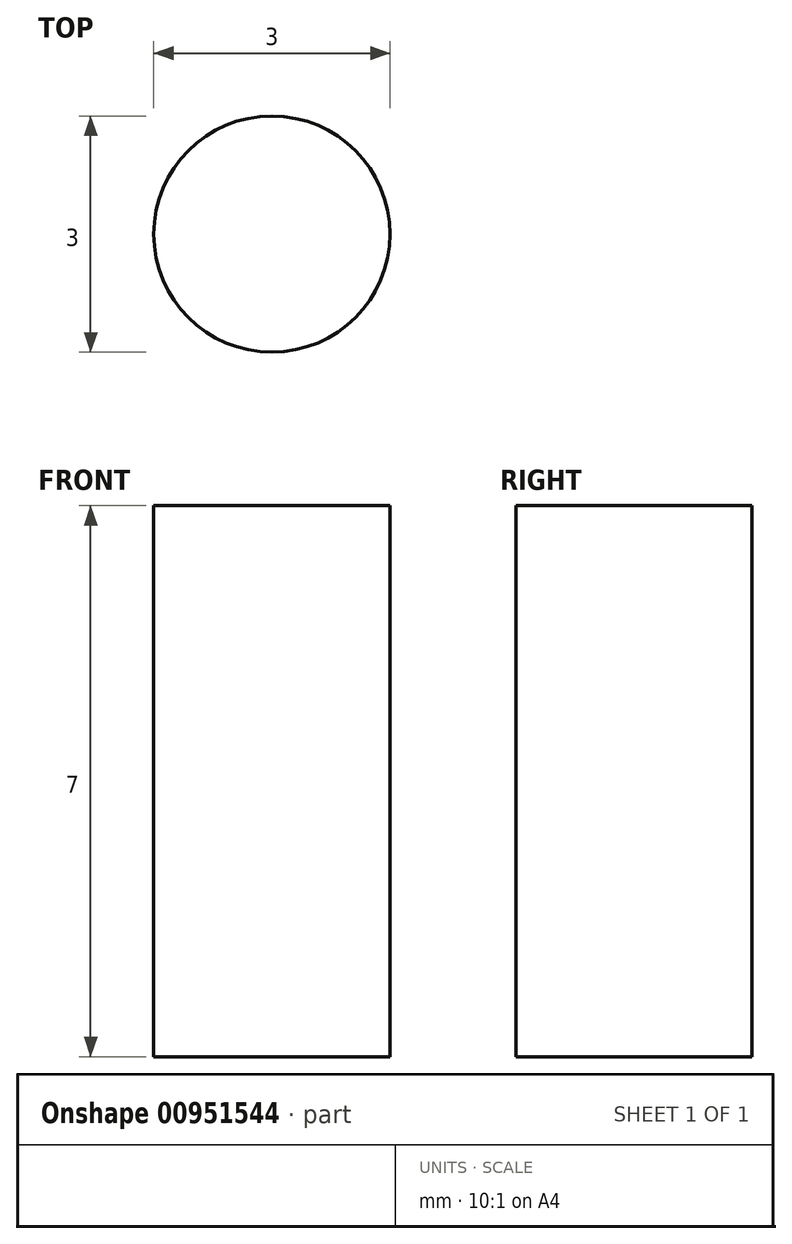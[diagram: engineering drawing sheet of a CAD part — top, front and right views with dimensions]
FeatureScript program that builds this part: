
annotation { "Feature Type Name" : "Feature", "Feature Type Description" : "" }
export const myFeature = defineFeature(function(context is Context, id is Id, definition is map)
    precondition{}
    {
        {
            var Q0;
            Q0=qCreatedBy(makeId("Top.planeOp"),FACE);
            var sketch = newSketch(context, id + "F0", { "sketchPlane" : qUnion([Q0])});
            skCircle(sketch, "E0", {"center": v(0, 0) * mm, "radius": 1.5 * mm});
            skSolve(sketch);
        }
        {
            var Q0;
            Q0 = qSketchRegion(id + "F0", true);
            extrude(context, id + "F1", {"entities" : qUnion([Q0]), "depth" : 7 * mm, "offsetDistance" : 25 * mm});
        }
    });
